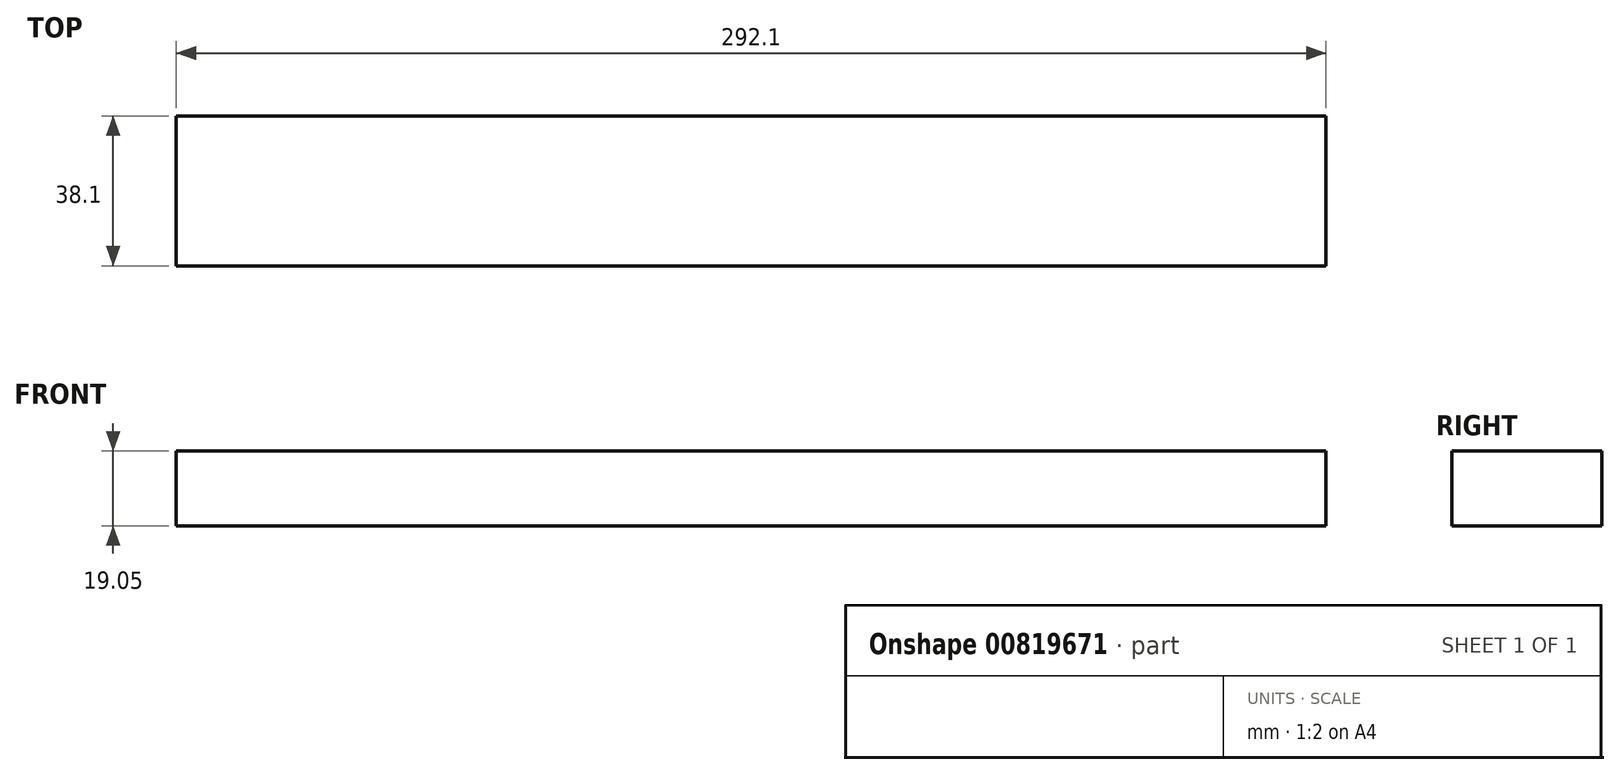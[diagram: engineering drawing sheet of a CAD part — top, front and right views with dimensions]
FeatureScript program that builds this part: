
annotation { "Feature Type Name" : "Feature", "Feature Type Description" : "" }
export const myFeature = defineFeature(function(context is Context, id is Id, definition is map)
    precondition{}
    {
        {
            var Q0;
            Q0=qCreatedBy(makeId("Front.planeOp"),FACE);
            var sketch = newSketch(context, id + "F0", { "sketchPlane" : qUnion([Q0])});
            skLineSegment(sketch, "E0.bottom", {"start": v(0, 0) * mm, "end": v(-292.1, 0) * mm});
            skLineSegment(sketch, "E0.top", {"start": v(0, 19.05) * mm, "end": v(-292.1, 19.05) * mm});
            skLineSegment(sketch, "E0.left", {"start": v(0, 0) * mm, "end": v(0, 19.05) * mm});
            skLineSegment(sketch, "E0.right", {"start": v(-292.1, 0) * mm, "end": v(-292.1, 19.05) * mm});
            skSolve(sketch);
        }
        {
            var Q0;
            Q0 = qSketchRegion(id + "F0", true);
            extrude(context, id + "F1", {"entities" : qUnion([Q0]), "flatOperationType" : FlatOperationType.REMOVE, "depth" : 38.1 * mm, "offsetDistance" : 25.4 * mm, "domain" : OperationDomain.MODEL});
        }
    });
